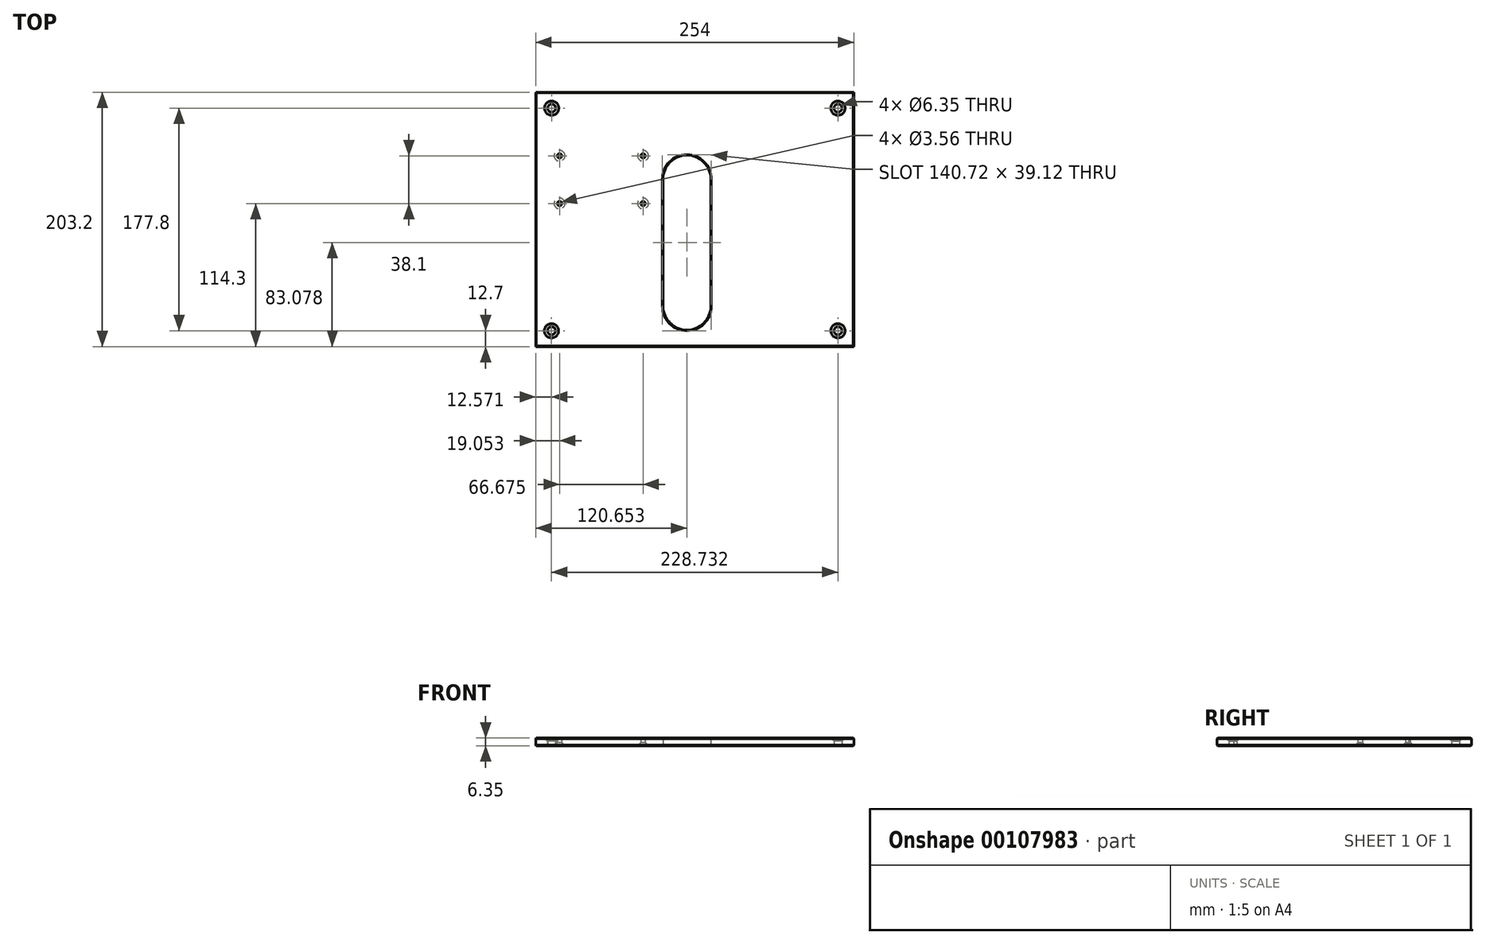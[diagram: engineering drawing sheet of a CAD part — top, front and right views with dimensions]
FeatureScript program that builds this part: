
annotation { "Feature Type Name" : "Feature", "Feature Type Description" : "" }
export const myFeature = defineFeature(function(context is Context, id is Id, definition is map)
    precondition{}
    {
        {
            var Q0;
            Q0=qCreatedBy(makeId("Top.planeOp"),FACE);
            var sketch = newSketch(context, id + "F0", { "sketchPlane" : qUnion([Q0])});
            skLineSegment(sketch, "E0.bottom", {"start": v(141.53, -101.6) * mm, "end": v(-112.47, -101.6) * mm});
            skLineSegment(sketch, "E0.top", {"start": v(141.53, 101.6) * mm, "end": v(-112.47, 101.6) * mm});
            skLineSegment(sketch, "E0.left", {"start": v(141.53, -101.6) * mm, "end": v(141.53, 101.6) * mm});
            skLineSegment(sketch, "E0.right", {"start": v(-112.47, -101.6) * mm, "end": v(-112.47, 101.6) * mm});
            skPoint(sketch, "E0.middle", {"position": v(22.23, -27.18) * mm});
            skArc(sketch, "E1", {"start": v(-10.87, -69.32) * mm, "mid": v(8.18, -88.37) * mm, "end": v(27.23, -69.32) * mm});
            skArc(sketch, "E2", {"start": v(27.23, 32.28) * mm, "mid": v(8.18, 51.33) * mm, "end": v(-10.87, 32.28) * mm});
            skLineSegment(sketch, "E3", {"start": v(-10.87, 32.28) * mm, "end": v(-10.87, -69.32) * mm});
            skLineSegment(sketch, "E4", {"start": v(27.23, -69.32) * mm, "end": v(27.23, 32.28) * mm});
            skLineSegment(sketch, "E5", {"start": v(-99.77, 88.9) * mm, "end": v(128.83, 88.9) * mm, "construction": true});
            skLineSegment(sketch, "E6", {"start": v(128.83, 88.9) * mm, "end": v(128.83, -88.9) * mm, "construction": true});
            skLineSegment(sketch, "E7", {"start": v(128.83, -88.9) * mm, "end": v(-99.9, -88.9) * mm, "construction": true});
            skCircle(sketch, "E8", {"center": v(-99.77, 88.9) * mm, "radius": 3.18 * mm});
            skCircle(sketch, "E9", {"center": v(128.83, 88.9) * mm, "radius": 3.18 * mm});
            skCircle(sketch, "E10", {"center": v(128.83, -88.9) * mm, "radius": 3.18 * mm});
            skCircle(sketch, "E11", {"center": v(-99.9, -88.9) * mm, "radius": 3.18 * mm});
            skLineSegment(sketch, "E12.bottom", {"start": v(-26.74, 12.7) * mm, "end": v(-93.42, 12.7) * mm, "construction": true});
            skLineSegment(sketch, "E12.top", {"start": v(-26.74, 50.8) * mm, "end": v(-93.42, 50.8) * mm, "construction": true});
            skLineSegment(sketch, "E12.left", {"start": v(-26.74, -3.3) * mm, "end": v(-26.74, 63.37) * mm, "construction": true});
            skLineSegment(sketch, "E12.right", {"start": v(-93.42, -3.3) * mm, "end": v(-93.42, 63.37) * mm, "construction": true});
            skPoint(sketch, "E12.middle", {"position": v(-60.08, 33.21) * mm});
            skCircle(sketch, "E13", {"center": v(-93.42, 50.8) * mm, "radius": 1.78 * mm});
            skCircle(sketch, "E14", {"center": v(-26.74, 50.8) * mm, "radius": 1.78 * mm});
            skCircle(sketch, "E15", {"center": v(-93.42, 12.7) * mm, "radius": 1.78 * mm});
            skCircle(sketch, "E16", {"center": v(-26.74, 12.7) * mm, "radius": 1.78 * mm});
            skSolve(sketch);
        }
        {
            var Q0;
            Q0=makeQuery(id+"F0.imprint","IMPRINT",FACE,{"disambiguationData":[TD([[makeQuery(id+"F0.imprint","IMPRINT",EDGE,{"derivedFrom":sQuery(id+"F0.wireOp",EDGE,"E0.bottom")}),-1.0]])]});
            extrude(context, id + "F1", {"entities" : qUnion([Q0]), "depth" : 6.35 * mm});
        }
        {
            var Q0;
            Q0=makeQuery(id+"F1.opExtrude","CAP_EDGE",EDGE,{"disambiguationData":[OSD([sQuery(id+"F0.wireOp",EDGE,"E0.left")])],"isStart":false});
            var Q1;
            Q1=makeQuery(id+"F1.opExtrude","CAP_EDGE",EDGE,{"disambiguationData":[OSD([sQuery(id+"F0.wireOp",EDGE,"E0.bottom")])],"isStart":false});
            var Q2;
            Q2=makeQuery(id+"F1.opExtrude","CAP_EDGE",EDGE,{"disambiguationData":[OSD([sQuery(id+"F0.wireOp",EDGE,"E0.top")])],"isStart":false});
            var Q3;
            Q3=makeQuery(id+"F1.opExtrude","CAP_EDGE",EDGE,{"disambiguationData":[OSD([sQuery(id+"F0.wireOp",EDGE,"E0.right")])],"isStart":false});
            var Q4;
            Q4=makeQuery(id+"F1.opExtrude","CAP_EDGE",EDGE,{"disambiguationData":[OSD([sQuery(id+"F0.wireOp",EDGE,"E0.right")])],"isStart":true});
            var Q5;
            Q5=makeQuery(id+"F1.opExtrude","CAP_EDGE",EDGE,{"disambiguationData":[OSD([sQuery(id+"F0.wireOp",EDGE,"E0.bottom")])],"isStart":true});
            var Q6;
            Q6=makeQuery(id+"F1.opExtrude","CAP_EDGE",EDGE,{"disambiguationData":[OSD([sQuery(id+"F0.wireOp",EDGE,"E0.left")])],"isStart":true});
            var Q7;
            Q7=makeQuery(id+"F1.opExtrude","CAP_EDGE",EDGE,{"disambiguationData":[OSD([sQuery(id+"F0.wireOp",EDGE,"E0.top")])],"isStart":true});
            var Q8;
            Q8=makeQuery(id+"F1.opExtrude","CAP_EDGE",EDGE,{"disambiguationData":[OSD([sQuery(id+"F0.wireOp",EDGE,"E3")])],"isStart":true});
            var Q9;
            Q9=makeQuery(id+"F1.opExtrude","CAP_EDGE",EDGE,{"disambiguationData":[OSD([sQuery(id+"F0.wireOp",EDGE,"E3")])],"isStart":false});
            var Q10;
            Q10=makeQuery(id+"F1.opExtrude","CAP_EDGE",EDGE,{"disambiguationData":[OSD([sQuery(id+"F0.wireOp",EDGE,"E11")])],"isStart":true});
            var Q11;
            Q11=makeQuery(id+"F1.opExtrude","CAP_EDGE",EDGE,{"disambiguationData":[OSD([sQuery(id+"F0.wireOp",EDGE,"E10")])],"isStart":true});
            var Q12;
            Q12=makeQuery(id+"F1.opExtrude","CAP_EDGE",EDGE,{"disambiguationData":[OSD([sQuery(id+"F0.wireOp",EDGE,"E9")])],"isStart":true});
            var Q13;
            Q13=makeQuery(id+"F1.opExtrude","CAP_EDGE",EDGE,{"disambiguationData":[OSD([sQuery(id+"F0.wireOp",EDGE,"E8")])],"isStart":true});
            chamfer(context, id + "F2", {"entities" : qUnion([Q0, Q1, Q2, Q3, Q4, Q5, Q6, Q7, Q8, Q9, Q10, Q11, Q12, Q13]), "width" : 0.5 * mm, "tangentPropagation" : true});
        }
        {
            var Q0;
            Q0=makeQuery(id+"F1.opExtrude","CAP_EDGE",EDGE,{"disambiguationData":[OSD([sQuery(id+"F0.wireOp",EDGE,"E8")])],"isStart":false});
            var Q1;
            Q1=makeQuery(id+"F1.opExtrude","CAP_EDGE",EDGE,{"disambiguationData":[OSD([sQuery(id+"F0.wireOp",EDGE,"E11")])],"isStart":false});
            var Q2;
            Q2=makeQuery(id+"F1.opExtrude","CAP_EDGE",EDGE,{"disambiguationData":[OSD([sQuery(id+"F0.wireOp",EDGE,"E9")])],"isStart":false});
            var Q3;
            Q3=makeQuery(id+"F1.opExtrude","CAP_EDGE",EDGE,{"disambiguationData":[OSD([sQuery(id+"F0.wireOp",EDGE,"E10")])],"isStart":false});
            var Q4;
            Q4=makeQuery(id+"F1.opExtrude","CAP_EDGE",EDGE,{"disambiguationData":[OSD([sQuery(id+"F0.wireOp",EDGE,"E15")])],"isStart":true});
            var Q5;
            Q5=makeQuery(id+"F1.opExtrude","CAP_EDGE",EDGE,{"disambiguationData":[OSD([sQuery(id+"F0.wireOp",EDGE,"E16")])],"isStart":true});
            var Q6;
            Q6=makeQuery(id+"F1.opExtrude","CAP_EDGE",EDGE,{"disambiguationData":[OSD([sQuery(id+"F0.wireOp",EDGE,"E14")])],"isStart":true});
            var Q7;
            Q7=makeQuery(id+"F1.opExtrude","CAP_EDGE",EDGE,{"disambiguationData":[OSD([sQuery(id+"F0.wireOp",EDGE,"E13")])],"isStart":true});
            chamfer(context, id + "F3", {"entities" : qUnion([Q0, Q1, Q2, Q3, Q4, Q5, Q6, Q7]), "width" : 2.54 * mm, "tangentPropagation" : true});
        }
    });
